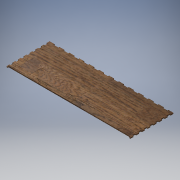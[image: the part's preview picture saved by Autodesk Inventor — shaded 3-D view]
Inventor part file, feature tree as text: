
AUTODESK INVENTOR PART (.ipt)
format: ipt  version: 2018.3 (Build 223284000, 284)  size: 1,935,360 bytes
history: native  units: mm
features: other x14, reference x10, extrude x5, sketch x5
ambient origin geometry x8: Origin, YZ Plane, XZ Plane, XY Plane, X Axis, Y Axis, Z Axis, Center Point
bodies: Solido1 (feature_tree)
feature tree (34):
  extrude  "Estrusione1"  Depth=467.0mm
  extrude  "Estrusione2"  Depth=157.0mm
  extrude  "Estrusione3"  Depth=4.0mm TaperAngle=0.0deg
  extrude  "Estrusione4"  Depth=4.0mm
  extrude  "Estrusione5"  Depth=475.0mm
  sketch  "Schizzo1"
  sketch  "Schizzo3"
  other  "Linea chiusa proiettata2"
  sketch  "Schizzo4"
  reference  "Riferimento1"
  reference  "Riferimento2"
  reference  "Riferimento3"
  reference  "Riferimento4"
  reference  "Riferimento5"
  reference  "Riferimento6"
  reference  "Riferimento7"
  sketch  "Schizzo5"
  reference  "Riferimento9"
  reference  "Riferimento11"
  reference  "Riferimento12"
  sketch  "Schizzo6"
  other  "<userpath>\Desktop\Scorbot Hardware\Case Board V2\caseHw v2.iam"
  other  "caseHw v2.iam"
  other  "matherBoard v1:1"
  other  "PCB Component:1"
  other  "Board:1"
  other  "Raspberry Pi 3:1"
  other  "Raspberry Pi 347_115"
  other  "Raspberry Pi 345_113"
  other  "Raspberry Pi 349_117"
  other  "Raspberry Pi 351_119"
  other  "Dietro:1"
  other  "LatoPy:1"
  other  "LatoAlimentatore:1"
